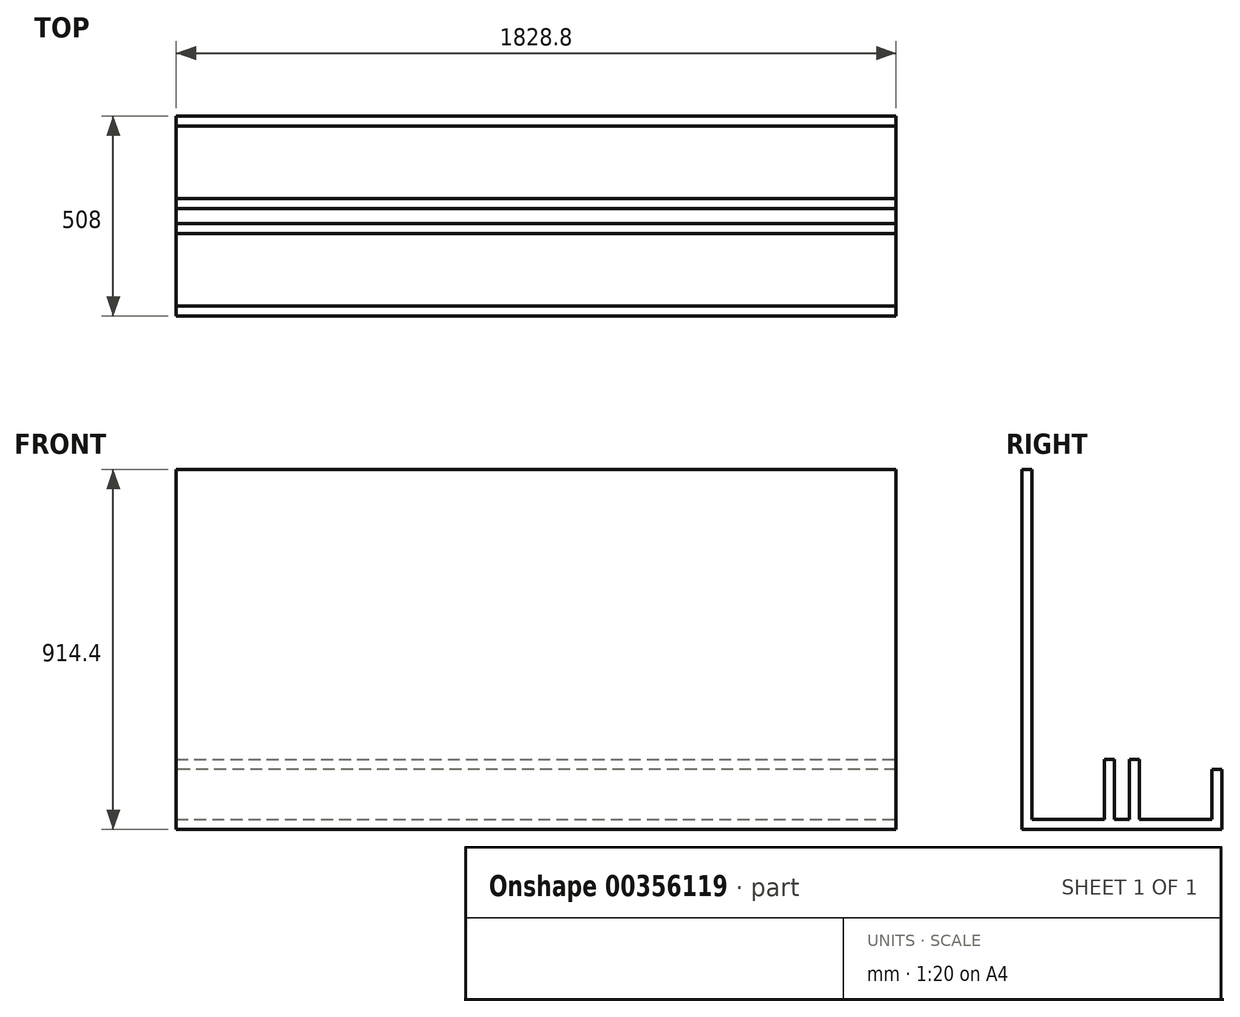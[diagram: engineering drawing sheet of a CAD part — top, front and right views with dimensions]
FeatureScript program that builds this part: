
annotation { "Feature Type Name" : "Feature", "Feature Type Description" : "" }
export const myFeature = defineFeature(function(context is Context, id is Id, definition is map)
    precondition{}
    {
        {
            var Q0;
            Q0=qCreatedBy(makeId("Right.planeOp"),FACE);
            var sketch = newSketch(context, id + "F0", { "sketchPlane" : qUnion([Q0])});
            skLineSegment(sketch, "E0.bottom", {"start": v(-254, 457.2) * mm, "end": v(-228.6, 457.2) * mm});
            skLineSegment(sketch, "E0.top", {"start": v(-254, -457.2) * mm, "end": v(254, -457.2) * mm});
            skLineSegment(sketch, "E0.left", {"start": v(-254, 457.2) * mm, "end": v(-254, -457.2) * mm});
            skPoint(sketch, "E0.middle", {"position": v(0, 0) * mm});
            skLineSegment(sketch, "E1.1", {"start": v(-228.6, -431.8) * mm, "end": v(228.6, -431.8) * mm});
            skLineSegment(sketch, "E1.2", {"start": v(-228.6, 457.2) * mm, "end": v(-228.6, -457.2) * mm});
            skLineSegment(sketch, "E2", {"start": v(228.6, -457.2) * mm, "end": v(228.6, -304.8) * mm});
            skLineSegment(sketch, "E3", {"start": v(228.6, -304.8) * mm, "end": v(254, -304.8) * mm});
            skLineSegment(sketch, "E4", {"start": v(254, -457.2) * mm, "end": v(254, -304.8) * mm});
            skSolve(sketch);
        }
        {
            var Q0;
            {var subQ2=sQuery(id+"F0.wireOp",EDGE,"E0.bottom");Q0=makeQuery(id+"F0.imprint","IMPRINT",FACE,{"disambiguationData":[TD([[makeQuery(id+"F0.imprint","IMPRINT",EDGE,{"derivedFrom":subQ2}),-1.0]])]});}
            var Q1;
            {var subQ5=sQuery(id+"F0.wireOp",EDGE,"E1.1");Q1=makeQuery(id+"F0.imprint","IMPRINT",FACE,{"disambiguationData":[TD([[makeQuery(id+"F0.imprint","IMPRINT",EDGE,{"derivedFrom":subQ5}),-1.0]])]});}
            var Q2;
            {var subQ0=sQuery(id+"F0.wireOp",EDGE,"E3");Q2=makeQuery(id+"F0.imprint","IMPRINT",FACE,{"disambiguationData":[TD([[makeQuery(id+"F0.imprint","IMPRINT",EDGE,{"derivedFrom":subQ0}),-1.0]])]});}
            extrude(context, id + "F1", {"entities" : qUnion([Q0, Q1, Q2]), "endBound" : BoundingType.SYMMETRIC, "depth" : 1828.8 * mm});
        }
        {
            var Q0;
            Q0=makeQuery(id+"F1.opExtrude","CAP_FACE",FACE,{"disambiguationData":[OSD([sQuery(id+"F0.wireOp",EDGE,"E0.bottom"),sQuery(id+"F0.wireOp",EDGE,"E0.top"),sQuery(id+"F0.wireOp",EDGE,"E0.left"),sQuery(id+"F0.wireOp",EDGE,"E1.1"),sQuery(id+"F0.wireOp",EDGE,"E1.2"),sQuery(id+"F0.wireOp",EDGE,"E2"),sQuery(id+"F0.wireOp",EDGE,"E3"),sQuery(id+"F0.wireOp",EDGE,"E4")])],"isStart":false});
            var sketch = newSketch(context, id + "F2", { "sketchPlane" : qUnion([Q0])});
            skLineSegment(sketch, "E5.bottom", {"start": v(-19.05, -431.8) * mm, "end": v(-44.45, -431.8) * mm});
            skLineSegment(sketch, "E5.top", {"start": v(-19.05, -279.4) * mm, "end": v(-44.45, -279.4) * mm});
            skLineSegment(sketch, "E5.left", {"start": v(-19.05, -431.8) * mm, "end": v(-19.05, -279.4) * mm});
            skLineSegment(sketch, "E5.right", {"start": v(-44.45, -431.8) * mm, "end": v(-44.45, -279.4) * mm});
            skLineSegment(sketch, "E6.bottom", {"start": v(19.05, -431.8) * mm, "end": v(44.45, -431.8) * mm});
            skLineSegment(sketch, "E6.top", {"start": v(19.05, -279.4) * mm, "end": v(44.45, -279.4) * mm});
            skLineSegment(sketch, "E6.left", {"start": v(19.05, -431.8) * mm, "end": v(19.05, -279.4) * mm});
            skLineSegment(sketch, "E6.right", {"start": v(44.45, -431.8) * mm, "end": v(44.45, -279.4) * mm});
            skSolve(sketch);
        }
        {
            var Q0;
            Q0=makeQuery(id+"F2.imprint","IMPRINT",FACE,{"disambiguationData":[TD([[makeQuery(id+"F2.imprint","IMPRINT",EDGE,{"derivedFrom":sQuery(id+"F2.wireOp",EDGE,"E5.bottom")}),1.0]])]});
            var Q1;
            Q1=makeQuery(id+"F2.imprint","IMPRINT",FACE,{"disambiguationData":[TD([[makeQuery(id+"F2.imprint","IMPRINT",EDGE,{"derivedFrom":sQuery(id+"F2.wireOp",EDGE,"E6.bottom")}),1.0]])]});
            extrude(context, id + "F3", {"entities" : qUnion([Q0, Q1]), "operationType" : NewBodyOperationType.ADD, "oppositeDirection" : true, "depth" : 1828.8 * mm});
        }
    });
